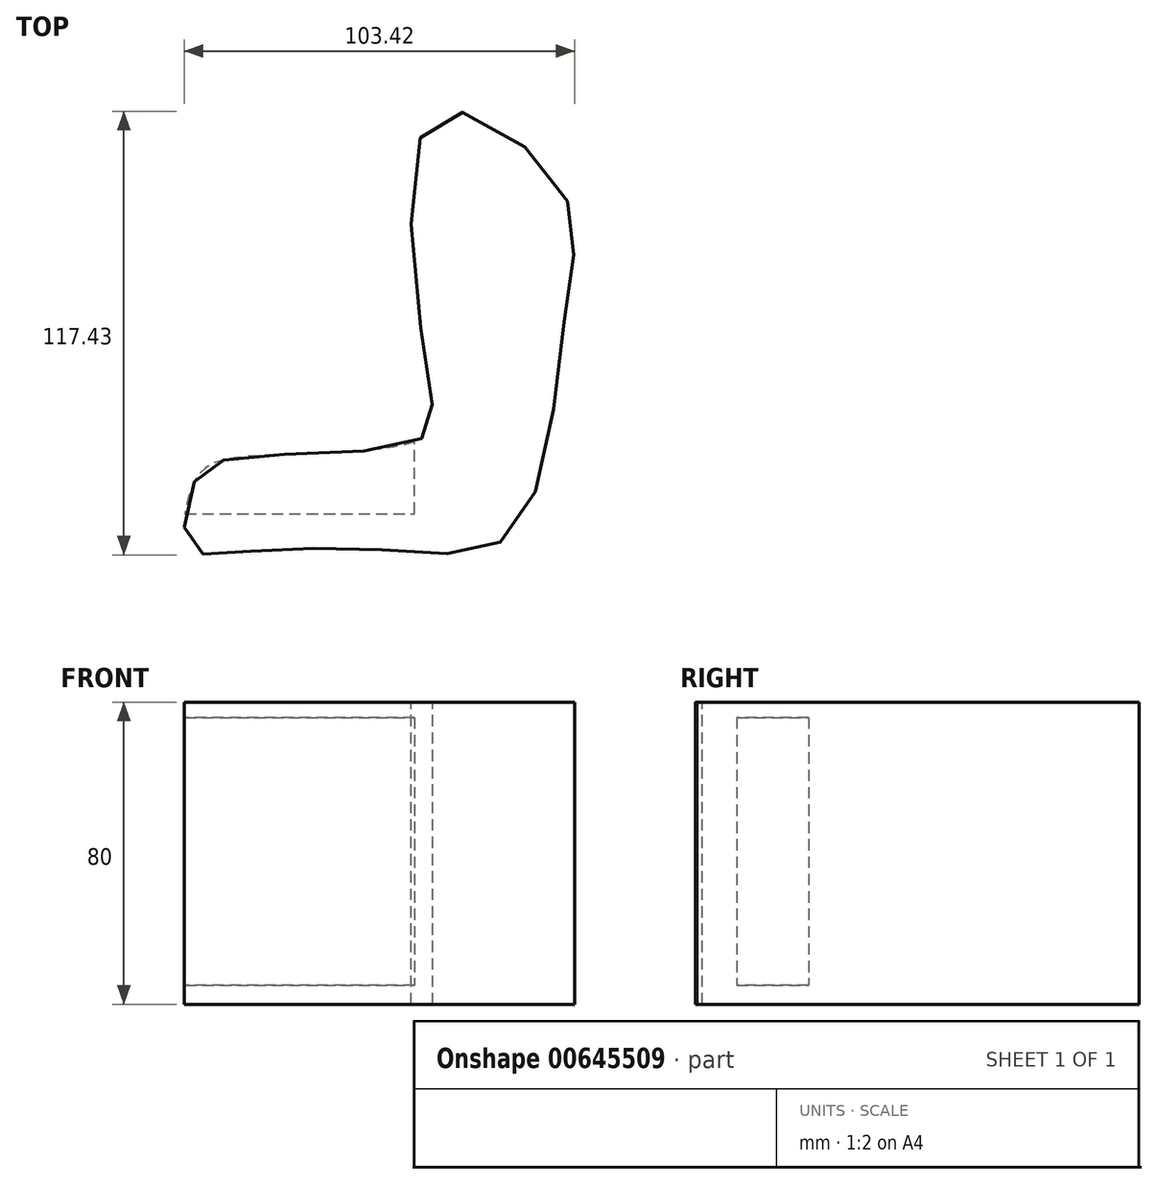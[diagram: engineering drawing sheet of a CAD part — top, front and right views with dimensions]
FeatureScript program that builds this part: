
annotation { "Feature Type Name" : "Feature", "Feature Type Description" : "" }
export const myFeature = defineFeature(function(context is Context, id is Id, definition is map)
    precondition{}
    {
        {
            var Q0;
            Q0=qCreatedBy(makeId("Top.planeOp"),FACE);
            var sketch = newSketch(context, id + "F0", { "sketchPlane" : qUnion([Q0])});
            skFitSpline(sketch, "E0", {"points": [v(-52.52, -60) * mm, v(-11.65, -60) * mm, v(17.36, -54.28) * mm, v(30.98, 5.05) * mm, v(29.23, 36.7) * mm, v(-3.74, 55.16) * mm, v(-5.5, -14.72) * mm, v(-8.13, -30.55) * mm, v(-54.28, -34.94) * mm, v(-67.46, -41.53) * mm, v(-68.78, -58.67) * mm, v(-52.52, -60) * mm]});
            skSolve(sketch);
        }
        {
            var Q0;
            Q0 = qSketchRegion(id + "F0", true);
            extrude(context, id + "F1", {"entities" : qUnion([Q0]), "depth" : 80 * mm, "offsetDistance" : 25.4 * mm});
        }
        {
            var Q0;
            Q0=qCreatedBy(makeId("Front.planeOp"),FACE);
            var sketch = newSketch(context, id + "F2", { "sketchPlane" : qUnion([Q0])});
            skLineSegment(sketch, "E1.bottom", {"start": v(-71.92, 5) * mm, "end": v(-9.16, 5) * mm});
            skLineSegment(sketch, "E1.top", {"start": v(-71.92, 75.92) * mm, "end": v(-9.16, 75.92) * mm});
            skLineSegment(sketch, "E1.left", {"start": v(-71.92, 5) * mm, "end": v(-71.92, 75.92) * mm});
            skLineSegment(sketch, "E1.right", {"start": v(-9.16, 5) * mm, "end": v(-9.16, 75.92) * mm});
            skSolve(sketch);
        }
        {
            var Q0;
            Q0 = qSketchRegion(id + "F2", true);
            extrude(context, id + "F3", {"entities" : qUnion([Q0]), "operationType" : NewBodyOperationType.REMOVE, "depth" : 50 * mm, "offsetDistance" : 25.4 * mm});
        }
    });
